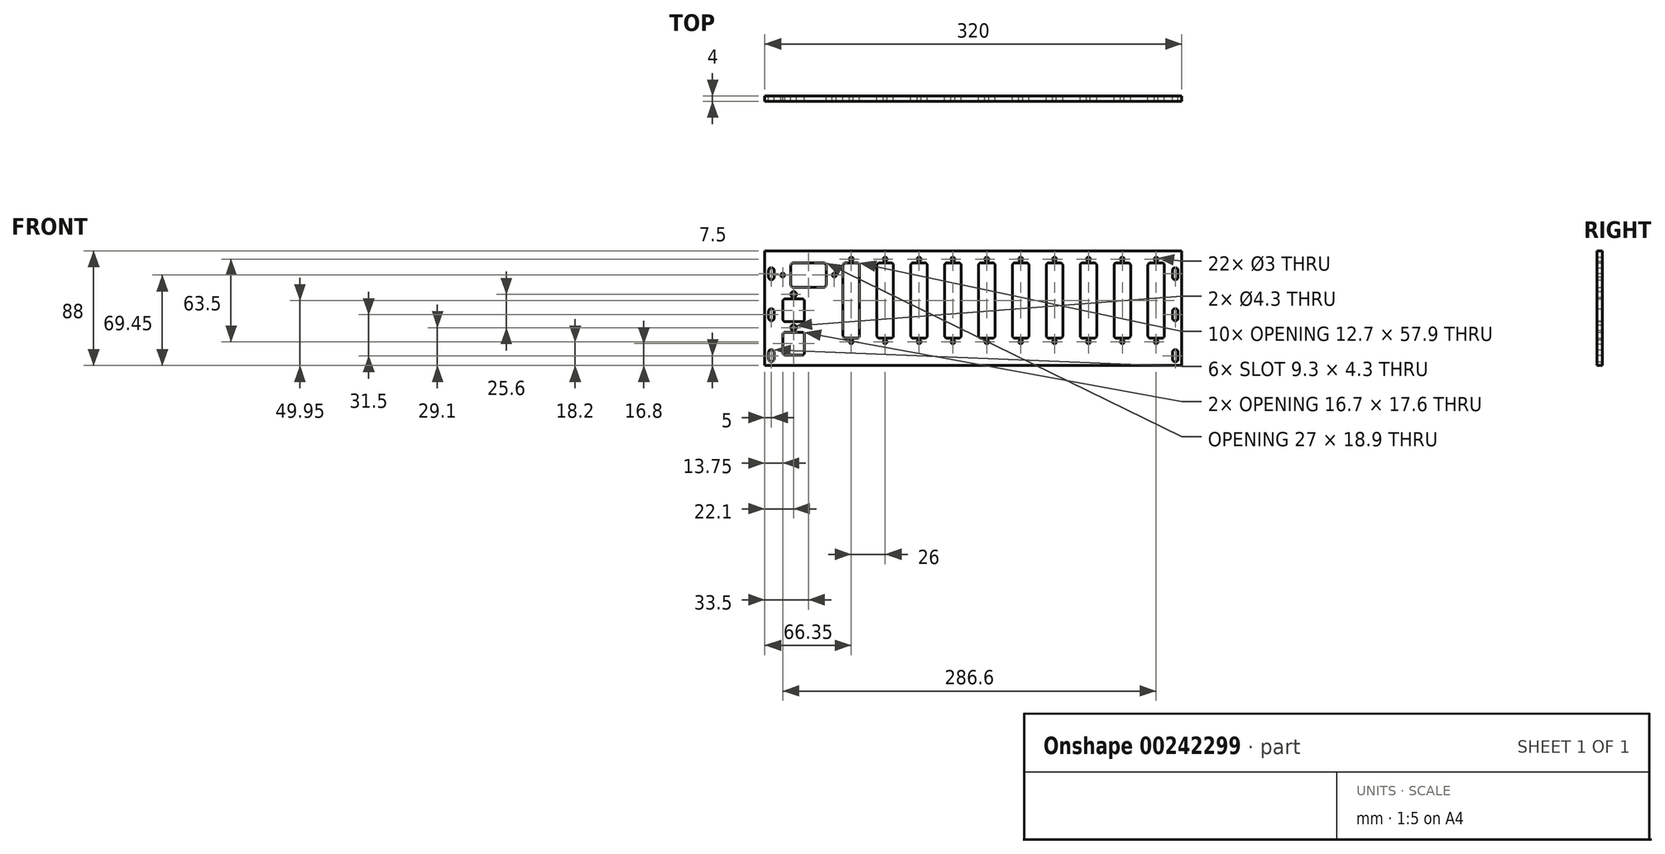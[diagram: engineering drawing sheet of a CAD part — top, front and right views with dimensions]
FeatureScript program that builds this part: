
annotation { "Feature Type Name" : "Feature", "Feature Type Description" : "" }
export const myFeature = defineFeature(function(context is Context, id is Id, definition is map)
    precondition{}
    {
        {
            var Q0;
            Q0=qCreatedBy(makeId("Front.planeOp"),FACE);
            var sketch = newSketch(context, id + "F0", { "sketchPlane" : qUnion([Q0])});
            skLineSegment(sketch, "E0.bottom", {"start": v(160, -44) * mm, "end": v(-160, -44) * mm});
            skLineSegment(sketch, "E0.top", {"start": v(160, 44) * mm, "end": v(-160, 44) * mm});
            skLineSegment(sketch, "E0.left", {"start": v(160, -44) * mm, "end": v(160, 44) * mm});
            skLineSegment(sketch, "E0.right", {"start": v(-160, -44) * mm, "end": v(-160, 44) * mm});
            skPoint(sketch, "E0.middle", {"position": v(0, 0) * mm});
            skLineSegment(sketch, "E1.bottom", {"start": v(-131.55, -36) * mm, "end": v(-144.25, -36) * mm});
            skLineSegment(sketch, "E1.top", {"start": v(-131.55, -18.4) * mm, "end": v(-144.25, -18.4) * mm});
            skLineSegment(sketch, "E1.left", {"start": v(-129.55, -34) * mm, "end": v(-129.55, -20.4) * mm});
            skLineSegment(sketch, "E1.right", {"start": v(-146.25, -34) * mm, "end": v(-146.25, -20.4) * mm});
            skPoint(sketch, "E1.middle", {"position": v(-137.9, -27.2) * mm});
            skLineSegment(sketch, "E2.0.1.0", {"start": v(-131.55, 7.2) * mm, "end": v(-144.25, 7.2) * mm});
            skLineSegment(sketch, "E2.0.1.1", {"start": v(-129.55, -8.4) * mm, "end": v(-129.55, 5.2) * mm});
            skLineSegment(sketch, "E2.0.1.2", {"start": v(-131.55, -10.4) * mm, "end": v(-144.25, -10.4) * mm});
            skLineSegment(sketch, "E2.0.1.3", {"start": v(-146.25, -8.4) * mm, "end": v(-146.25, 5.2) * mm});
            skLineSegment(sketch, "E2.direction1", {"start": v(-146.25, -18.4) * mm, "end": v(-121.25, -18.4) * mm, "construction": true});
            skLineSegment(sketch, "E2.direction2", {"start": v(-146.25, -18.4) * mm, "end": v(-146.25, 7.2) * mm, "construction": true});
            skLineSegment(sketch, "E3.bottom", {"start": v(-115, 16) * mm, "end": v(-138, 16) * mm});
            skLineSegment(sketch, "E3.top", {"start": v(-115, 34.9) * mm, "end": v(-138, 34.9) * mm});
            skLineSegment(sketch, "E3.left", {"start": v(-113, 18) * mm, "end": v(-113, 32.9) * mm});
            skLineSegment(sketch, "E3.right", {"start": v(-140, 18) * mm, "end": v(-140, 32.9) * mm});
            skPoint(sketch, "E3.middle", {"position": v(-126.5, 25.45) * mm});
            skCircle(sketch, "E4", {"center": v(-146.25, 25.45) * mm, "radius": 1.5 * mm});
            skCircle(sketch, "E5", {"center": v(-106.75, 25.45) * mm, "radius": 1.5 * mm});
            skLineSegment(sketch, "E6.bottom", {"start": v(-98, -23) * mm, "end": v(-89.3, -23) * mm});
            skLineSegment(sketch, "E6.top", {"start": v(-98, 34.9) * mm, "end": v(-89.3, 34.9) * mm});
            skLineSegment(sketch, "E6.left", {"start": v(-100, -21) * mm, "end": v(-100, 32.9) * mm});
            skLineSegment(sketch, "E6.right", {"start": v(-87.3, -21) * mm, "end": v(-87.3, 32.9) * mm});
            skCircle(sketch, "E7", {"center": v(-93.65, -25.8) * mm, "radius": 1.5 * mm});
            skPoint(sketch, "E7.centerSnap0", {"position": v(-93.65, -23) * mm});
            skCircle(sketch, "E8", {"center": v(-93.65, 37.7) * mm, "radius": 1.5 * mm});
            skPoint(sketch, "E8.centerSnap0", {"position": v(-93.65, 34.9) * mm});
            skCircle(sketch, "E9.1.0.0", {"center": v(-67.65, 37.7) * mm, "radius": 1.5 * mm});
            skLineSegment(sketch, "E9.1.0.1", {"start": v(-72, 34.9) * mm, "end": v(-63.3, 34.9) * mm});
            skLineSegment(sketch, "E9.1.0.2", {"start": v(-74, -21) * mm, "end": v(-74, 32.9) * mm});
            skLineSegment(sketch, "E9.1.0.3", {"start": v(-61.3, -21) * mm, "end": v(-61.3, 32.9) * mm});
            skLineSegment(sketch, "E9.1.0.4", {"start": v(-72, -23) * mm, "end": v(-63.3, -23) * mm});
            skCircle(sketch, "E9.1.0.5", {"center": v(-67.65, -25.8) * mm, "radius": 1.5 * mm});
            skCircle(sketch, "E9.2.0.0", {"center": v(-41.65, 37.7) * mm, "radius": 1.5 * mm});
            skLineSegment(sketch, "E9.2.0.1", {"start": v(-46, 34.9) * mm, "end": v(-37.3, 34.9) * mm});
            skLineSegment(sketch, "E9.2.0.2", {"start": v(-48, -21) * mm, "end": v(-48, 32.9) * mm});
            skLineSegment(sketch, "E9.2.0.3", {"start": v(-35.3, -21) * mm, "end": v(-35.3, 32.9) * mm});
            skLineSegment(sketch, "E9.2.0.4", {"start": v(-46, -23) * mm, "end": v(-37.3, -23) * mm});
            skCircle(sketch, "E9.2.0.5", {"center": v(-41.65, -25.8) * mm, "radius": 1.5 * mm});
            skCircle(sketch, "E9.3.0.0", {"center": v(-15.65, 37.7) * mm, "radius": 1.5 * mm});
            skLineSegment(sketch, "E9.3.0.1", {"start": v(-20, 34.9) * mm, "end": v(-11.3, 34.9) * mm});
            skLineSegment(sketch, "E9.3.0.2", {"start": v(-22, -21) * mm, "end": v(-22, 32.9) * mm});
            skLineSegment(sketch, "E9.3.0.3", {"start": v(-9.3, -21) * mm, "end": v(-9.3, 32.9) * mm});
            skLineSegment(sketch, "E9.3.0.4", {"start": v(-20, -23) * mm, "end": v(-11.3, -23) * mm});
            skCircle(sketch, "E9.3.0.5", {"center": v(-15.65, -25.8) * mm, "radius": 1.5 * mm});
            skCircle(sketch, "E9.4.0.0", {"center": v(10.35, 37.7) * mm, "radius": 1.5 * mm});
            skLineSegment(sketch, "E9.4.0.1", {"start": v(6, 34.9) * mm, "end": v(14.7, 34.9) * mm});
            skLineSegment(sketch, "E9.4.0.2", {"start": v(4, -21) * mm, "end": v(4, 32.9) * mm});
            skLineSegment(sketch, "E9.4.0.3", {"start": v(16.7, -21) * mm, "end": v(16.7, 32.9) * mm});
            skLineSegment(sketch, "E9.4.0.4", {"start": v(6, -23) * mm, "end": v(14.7, -23) * mm});
            skCircle(sketch, "E9.4.0.5", {"center": v(10.35, -25.8) * mm, "radius": 1.5 * mm});
            skCircle(sketch, "E9.5.0.0", {"center": v(36.35, 37.7) * mm, "radius": 1.5 * mm});
            skLineSegment(sketch, "E9.5.0.1", {"start": v(32, 34.9) * mm, "end": v(40.7, 34.9) * mm});
            skLineSegment(sketch, "E9.5.0.2", {"start": v(30, -21) * mm, "end": v(30, 32.9) * mm});
            skLineSegment(sketch, "E9.5.0.3", {"start": v(42.7, -21) * mm, "end": v(42.7, 32.9) * mm});
            skLineSegment(sketch, "E9.5.0.4", {"start": v(32, -23) * mm, "end": v(40.7, -23) * mm});
            skCircle(sketch, "E9.5.0.5", {"center": v(36.35, -25.8) * mm, "radius": 1.5 * mm});
            skCircle(sketch, "E9.6.0.0", {"center": v(62.35, 37.7) * mm, "radius": 1.5 * mm});
            skLineSegment(sketch, "E9.6.0.1", {"start": v(58, 34.9) * mm, "end": v(66.7, 34.9) * mm});
            skLineSegment(sketch, "E9.6.0.2", {"start": v(56, -21) * mm, "end": v(56, 32.9) * mm});
            skLineSegment(sketch, "E9.6.0.3", {"start": v(68.7, -21) * mm, "end": v(68.7, 32.9) * mm});
            skLineSegment(sketch, "E9.6.0.4", {"start": v(58, -23) * mm, "end": v(66.7, -23) * mm});
            skCircle(sketch, "E9.6.0.5", {"center": v(62.35, -25.8) * mm, "radius": 1.5 * mm});
            skCircle(sketch, "E9.7.0.0", {"center": v(88.35, 37.7) * mm, "radius": 1.5 * mm});
            skLineSegment(sketch, "E9.7.0.1", {"start": v(84, 34.9) * mm, "end": v(92.7, 34.9) * mm});
            skLineSegment(sketch, "E9.7.0.2", {"start": v(82, -21) * mm, "end": v(82, 32.9) * mm});
            skLineSegment(sketch, "E9.7.0.3", {"start": v(94.7, -21) * mm, "end": v(94.7, 32.9) * mm});
            skLineSegment(sketch, "E9.7.0.4", {"start": v(84, -23) * mm, "end": v(92.7, -23) * mm});
            skCircle(sketch, "E9.7.0.5", {"center": v(88.35, -25.8) * mm, "radius": 1.5 * mm});
            skCircle(sketch, "E9.8.0.0", {"center": v(114.35, 37.7) * mm, "radius": 1.5 * mm});
            skLineSegment(sketch, "E9.8.0.1", {"start": v(110, 34.9) * mm, "end": v(118.7, 34.9) * mm});
            skLineSegment(sketch, "E9.8.0.2", {"start": v(108, -21) * mm, "end": v(108, 32.9) * mm});
            skLineSegment(sketch, "E9.8.0.3", {"start": v(120.7, -21) * mm, "end": v(120.7, 32.9) * mm});
            skLineSegment(sketch, "E9.8.0.4", {"start": v(110, -23) * mm, "end": v(118.7, -23) * mm});
            skCircle(sketch, "E9.8.0.5", {"center": v(114.35, -25.8) * mm, "radius": 1.5 * mm});
            skCircle(sketch, "E9.9.0.0", {"center": v(140.35, 37.7) * mm, "radius": 1.5 * mm});
            skLineSegment(sketch, "E9.9.0.1", {"start": v(136, 34.9) * mm, "end": v(144.7, 34.9) * mm});
            skLineSegment(sketch, "E9.9.0.2", {"start": v(134, -21) * mm, "end": v(134, 32.9) * mm});
            skLineSegment(sketch, "E9.9.0.3", {"start": v(146.7, -21) * mm, "end": v(146.7, 32.9) * mm});
            skLineSegment(sketch, "E9.9.0.4", {"start": v(136, -23) * mm, "end": v(144.7, -23) * mm});
            skCircle(sketch, "E9.9.0.5", {"center": v(140.35, -25.8) * mm, "radius": 1.5 * mm});
            skLineSegment(sketch, "E9.direction1", {"start": v(-93.65, 37.7) * mm, "end": v(-67.65, 37.7) * mm, "construction": true});
            skPoint(sketch, "E10.visualSharp", {"position": v(-100, 34.9) * mm});
            skArc(sketch, "E10.filletArc", {"start": v(-98, 34.9) * mm, "mid": v(-99.41, 34.31) * mm, "end": v(-100, 32.9) * mm});
            skPoint(sketch, "E11.visualSharp", {"position": v(-87.3, 34.9) * mm});
            skArc(sketch, "E11.filletArc", {"start": v(-87.3, 32.9) * mm, "mid": v(-87.89, 34.31) * mm, "end": v(-89.3, 34.9) * mm});
            skPoint(sketch, "E12.visualSharp", {"position": v(-100, -23) * mm});
            skArc(sketch, "E12.filletArc", {"start": v(-100, -21) * mm, "mid": v(-99.41, -22.41) * mm, "end": v(-98, -23) * mm});
            skPoint(sketch, "E13.visualSharp", {"position": v(-87.3, -23) * mm});
            skArc(sketch, "E13.filletArc", {"start": v(-89.3, -23) * mm, "mid": v(-87.89, -22.41) * mm, "end": v(-87.3, -21) * mm});
            skPoint(sketch, "E14.visualSharp", {"position": v(-74, 34.9) * mm});
            skArc(sketch, "E14.filletArc", {"start": v(-72, 34.9) * mm, "mid": v(-73.41, 34.31) * mm, "end": v(-74, 32.9) * mm});
            skPoint(sketch, "E15.visualSharp", {"position": v(-61.3, 34.9) * mm});
            skArc(sketch, "E15.filletArc", {"start": v(-61.3, 32.9) * mm, "mid": v(-61.89, 34.31) * mm, "end": v(-63.3, 34.9) * mm});
            skPoint(sketch, "E16.visualSharp", {"position": v(-61.3, -23) * mm});
            skArc(sketch, "E16.filletArc", {"start": v(-63.3, -23) * mm, "mid": v(-61.89, -22.41) * mm, "end": v(-61.3, -21) * mm});
            skPoint(sketch, "E17.visualSharp", {"position": v(-74, -23) * mm});
            skArc(sketch, "E17.filletArc", {"start": v(-74, -21) * mm, "mid": v(-73.41, -22.41) * mm, "end": v(-72, -23) * mm});
            skPoint(sketch, "E18.visualSharp", {"position": v(-48, 34.9) * mm});
            skArc(sketch, "E18.filletArc", {"start": v(-46, 34.9) * mm, "mid": v(-47.41, 34.31) * mm, "end": v(-48, 32.9) * mm});
            skPoint(sketch, "E19.visualSharp", {"position": v(-35.3, 34.9) * mm});
            skArc(sketch, "E19.filletArc", {"start": v(-35.3, 32.9) * mm, "mid": v(-35.89, 34.31) * mm, "end": v(-37.3, 34.9) * mm});
            skPoint(sketch, "E20.visualSharp", {"position": v(-35.3, -23) * mm});
            skArc(sketch, "E20.filletArc", {"start": v(-37.3, -23) * mm, "mid": v(-35.89, -22.41) * mm, "end": v(-35.3, -21) * mm});
            skPoint(sketch, "E21.visualSharp", {"position": v(-48, -23) * mm});
            skArc(sketch, "E21.filletArc", {"start": v(-48, -21) * mm, "mid": v(-47.41, -22.41) * mm, "end": v(-46, -23) * mm});
            skPoint(sketch, "E22.visualSharp", {"position": v(-22, -23) * mm});
            skArc(sketch, "E22.filletArc", {"start": v(-22, -21) * mm, "mid": v(-21.41, -22.41) * mm, "end": v(-20, -23) * mm});
            skPoint(sketch, "E23.visualSharp", {"position": v(-9.3, -23) * mm});
            skArc(sketch, "E23.filletArc", {"start": v(-11.3, -23) * mm, "mid": v(-9.89, -22.41) * mm, "end": v(-9.3, -21) * mm});
            skPoint(sketch, "E24.visualSharp", {"position": v(-9.3, 34.9) * mm});
            skArc(sketch, "E24.filletArc", {"start": v(-9.3, 32.9) * mm, "mid": v(-9.89, 34.31) * mm, "end": v(-11.3, 34.9) * mm});
            skPoint(sketch, "E25.visualSharp", {"position": v(-22, 34.9) * mm});
            skArc(sketch, "E25.filletArc", {"start": v(-20, 34.9) * mm, "mid": v(-21.41, 34.31) * mm, "end": v(-22, 32.9) * mm});
            skPoint(sketch, "E26.visualSharp", {"position": v(4, 34.9) * mm});
            skArc(sketch, "E26.filletArc", {"start": v(6, 34.9) * mm, "mid": v(4.59, 34.31) * mm, "end": v(4, 32.9) * mm});
            skPoint(sketch, "E27.visualSharp", {"position": v(16.7, 34.9) * mm});
            skArc(sketch, "E27.filletArc", {"start": v(16.7, 32.9) * mm, "mid": v(16.11, 34.31) * mm, "end": v(14.7, 34.9) * mm});
            skPoint(sketch, "E28.visualSharp", {"position": v(16.7, -23) * mm});
            skArc(sketch, "E28.filletArc", {"start": v(14.7, -23) * mm, "mid": v(16.11, -22.41) * mm, "end": v(16.7, -21) * mm});
            skPoint(sketch, "E29.visualSharp", {"position": v(4, -23) * mm});
            skArc(sketch, "E29.filletArc", {"start": v(4, -21) * mm, "mid": v(4.59, -22.41) * mm, "end": v(6, -23) * mm});
            skPoint(sketch, "E30.visualSharp", {"position": v(30, 34.9) * mm});
            skArc(sketch, "E30.filletArc", {"start": v(32, 34.9) * mm, "mid": v(30.59, 34.31) * mm, "end": v(30, 32.9) * mm});
            skPoint(sketch, "E31.visualSharp", {"position": v(42.7, 34.9) * mm});
            skArc(sketch, "E31.filletArc", {"start": v(42.7, 32.9) * mm, "mid": v(42.11, 34.31) * mm, "end": v(40.7, 34.9) * mm});
            skPoint(sketch, "E32.visualSharp", {"position": v(42.7, -23) * mm});
            skArc(sketch, "E32.filletArc", {"start": v(40.7, -23) * mm, "mid": v(42.11, -22.41) * mm, "end": v(42.7, -21) * mm});
            skPoint(sketch, "E33.visualSharp", {"position": v(30, -23) * mm});
            skArc(sketch, "E33.filletArc", {"start": v(30, -21) * mm, "mid": v(30.59, -22.41) * mm, "end": v(32, -23) * mm});
            skPoint(sketch, "E34.visualSharp", {"position": v(56, 34.9) * mm});
            skArc(sketch, "E34.filletArc", {"start": v(58, 34.9) * mm, "mid": v(56.59, 34.31) * mm, "end": v(56, 32.9) * mm});
            skPoint(sketch, "E35.visualSharp", {"position": v(68.7, 34.9) * mm});
            skArc(sketch, "E35.filletArc", {"start": v(68.7, 32.9) * mm, "mid": v(68.11, 34.31) * mm, "end": v(66.7, 34.9) * mm});
            skPoint(sketch, "E36.visualSharp", {"position": v(68.7, -23) * mm});
            skArc(sketch, "E36.filletArc", {"start": v(66.7, -23) * mm, "mid": v(68.11, -22.41) * mm, "end": v(68.7, -21) * mm});
            skPoint(sketch, "E37.visualSharp", {"position": v(56, -23) * mm});
            skArc(sketch, "E37.filletArc", {"start": v(56, -21) * mm, "mid": v(56.59, -22.41) * mm, "end": v(58, -23) * mm});
            skPoint(sketch, "E38.visualSharp", {"position": v(146.7, -23) * mm});
            skArc(sketch, "E38.filletArc", {"start": v(144.7, -23) * mm, "mid": v(146.11, -22.41) * mm, "end": v(146.7, -21) * mm});
            skPoint(sketch, "E39.visualSharp", {"position": v(146.7, 34.9) * mm});
            skArc(sketch, "E39.filletArc", {"start": v(146.7, 32.9) * mm, "mid": v(146.11, 34.31) * mm, "end": v(144.7, 34.9) * mm});
            skPoint(sketch, "E40.visualSharp", {"position": v(134, 34.9) * mm});
            skArc(sketch, "E40.filletArc", {"start": v(136, 34.9) * mm, "mid": v(134.59, 34.31) * mm, "end": v(134, 32.9) * mm});
            skPoint(sketch, "E41.visualSharp", {"position": v(134, -23) * mm});
            skArc(sketch, "E41.filletArc", {"start": v(134, -21) * mm, "mid": v(134.59, -22.41) * mm, "end": v(136, -23) * mm});
            skPoint(sketch, "E42.visualSharp", {"position": v(120.7, -23) * mm});
            skArc(sketch, "E42.filletArc", {"start": v(118.7, -23) * mm, "mid": v(120.11, -22.41) * mm, "end": v(120.7, -21) * mm});
            skPoint(sketch, "E43.visualSharp", {"position": v(108, -23) * mm});
            skArc(sketch, "E43.filletArc", {"start": v(108, -21) * mm, "mid": v(108.59, -22.41) * mm, "end": v(110, -23) * mm});
            skPoint(sketch, "E44.visualSharp", {"position": v(82, -23) * mm});
            skArc(sketch, "E44.filletArc", {"start": v(82, -21) * mm, "mid": v(82.59, -22.41) * mm, "end": v(84, -23) * mm});
            skPoint(sketch, "E45.visualSharp", {"position": v(82, 34.9) * mm});
            skArc(sketch, "E45.filletArc", {"start": v(84, 34.9) * mm, "mid": v(82.59, 34.31) * mm, "end": v(82, 32.9) * mm});
            skPoint(sketch, "E46.visualSharp", {"position": v(108, 34.9) * mm});
            skArc(sketch, "E46.filletArc", {"start": v(110, 34.9) * mm, "mid": v(108.59, 34.31) * mm, "end": v(108, 32.9) * mm});
            skPoint(sketch, "E47.visualSharp", {"position": v(120.7, 34.9) * mm});
            skArc(sketch, "E47.filletArc", {"start": v(120.7, 32.9) * mm, "mid": v(120.11, 34.31) * mm, "end": v(118.7, 34.9) * mm});
            skPoint(sketch, "E48.visualSharp", {"position": v(94.7, 34.9) * mm});
            skArc(sketch, "E48.filletArc", {"start": v(94.7, 32.9) * mm, "mid": v(94.11, 34.31) * mm, "end": v(92.7, 34.9) * mm});
            skPoint(sketch, "E49.visualSharp", {"position": v(94.7, -23) * mm});
            skArc(sketch, "E49.filletArc", {"start": v(92.7, -23) * mm, "mid": v(94.11, -22.41) * mm, "end": v(94.7, -21) * mm});
            skPoint(sketch, "E50.visualSharp", {"position": v(-113, 34.9) * mm});
            skArc(sketch, "E50.filletArc", {"start": v(-113, 32.9) * mm, "mid": v(-113.59, 34.31) * mm, "end": v(-115, 34.9) * mm});
            skPoint(sketch, "E51.visualSharp", {"position": v(-140, 34.9) * mm});
            skArc(sketch, "E51.filletArc", {"start": v(-138, 34.9) * mm, "mid": v(-139.41, 34.31) * mm, "end": v(-140, 32.9) * mm});
            skPoint(sketch, "E52.visualSharp", {"position": v(-140, 16) * mm});
            skArc(sketch, "E52.filletArc", {"start": v(-140, 18) * mm, "mid": v(-139.41, 16.59) * mm, "end": v(-138, 16) * mm});
            skPoint(sketch, "E53.visualSharp", {"position": v(-113, 16) * mm});
            skArc(sketch, "E53.filletArc", {"start": v(-115, 16) * mm, "mid": v(-113.59, 16.59) * mm, "end": v(-113, 18) * mm});
            skPoint(sketch, "E54.visualSharp", {"position": v(-129.55, 7.2) * mm});
            skArc(sketch, "E54.filletArc", {"start": v(-129.55, 5.2) * mm, "mid": v(-130.14, 6.61) * mm, "end": v(-131.55, 7.2) * mm});
            skPoint(sketch, "E55.visualSharp", {"position": v(-146.25, 7.2) * mm});
            skArc(sketch, "E55.filletArc", {"start": v(-144.25, 7.2) * mm, "mid": v(-145.66, 6.61) * mm, "end": v(-146.25, 5.2) * mm});
            skPoint(sketch, "E56.visualSharp", {"position": v(-146.25, -10.4) * mm});
            skArc(sketch, "E56.filletArc", {"start": v(-146.25, -8.4) * mm, "mid": v(-145.66, -9.81) * mm, "end": v(-144.25, -10.4) * mm});
            skPoint(sketch, "E57.visualSharp", {"position": v(-129.55, -10.4) * mm});
            skArc(sketch, "E57.filletArc", {"start": v(-131.55, -10.4) * mm, "mid": v(-130.14, -9.81) * mm, "end": v(-129.55, -8.4) * mm});
            skPoint(sketch, "E58.visualSharp", {"position": v(-129.55, -18.4) * mm});
            skArc(sketch, "E58.filletArc", {"start": v(-129.55, -20.4) * mm, "mid": v(-130.14, -18.99) * mm, "end": v(-131.55, -18.4) * mm});
            skPoint(sketch, "E59.visualSharp", {"position": v(-146.25, -18.4) * mm});
            skArc(sketch, "E59.filletArc", {"start": v(-144.25, -18.4) * mm, "mid": v(-145.66, -18.99) * mm, "end": v(-146.25, -20.4) * mm});
            skPoint(sketch, "E60.visualSharp", {"position": v(-146.25, -36) * mm});
            skArc(sketch, "E60.filletArc", {"start": v(-146.25, -34) * mm, "mid": v(-145.66, -35.41) * mm, "end": v(-144.25, -36) * mm});
            skPoint(sketch, "E61.visualSharp", {"position": v(-129.55, -36) * mm});
            skArc(sketch, "E61.filletArc", {"start": v(-131.55, -36) * mm, "mid": v(-130.14, -35.41) * mm, "end": v(-129.55, -34) * mm});
            skLineSegment(sketch, "E62", {"start": v(-152.85, -39) * mm, "end": v(-152.85, -34) * mm});
            skLineSegment(sketch, "E63", {"start": v(-157.15, -34) * mm, "end": v(-157.15, -39) * mm});
            skArc(sketch, "E64", {"start": v(-152.85, -34) * mm, "mid": v(-155, -31.85) * mm, "end": v(-157.15, -34) * mm});
            skArc(sketch, "E65", {"start": v(-157.15, -39) * mm, "mid": v(-155, -41.15) * mm, "end": v(-152.85, -39) * mm});
            skLineSegment(sketch, "E66.0.1.0", {"start": v(-152.85, -7.5) * mm, "end": v(-152.85, -2.5) * mm});
            skArc(sketch, "E66.0.1.1", {"start": v(-152.85, -2.5) * mm, "mid": v(-155, -0.35) * mm, "end": v(-157.15, -2.5) * mm});
            skLineSegment(sketch, "E66.0.1.2", {"start": v(-157.15, -2.5) * mm, "end": v(-157.15, -7.5) * mm});
            skArc(sketch, "E66.0.1.3", {"start": v(-157.15, -7.5) * mm, "mid": v(-155, -9.65) * mm, "end": v(-152.85, -7.5) * mm});
            skLineSegment(sketch, "E66.1.0.0", {"start": v(157.15, -39) * mm, "end": v(157.15, -34) * mm});
            skArc(sketch, "E66.1.0.1", {"start": v(157.15, -34) * mm, "mid": v(155, -31.85) * mm, "end": v(152.85, -34) * mm});
            skLineSegment(sketch, "E66.1.0.2", {"start": v(152.85, -34) * mm, "end": v(152.85, -39) * mm});
            skArc(sketch, "E66.1.0.3", {"start": v(152.85, -39) * mm, "mid": v(155, -41.15) * mm, "end": v(157.15, -39) * mm});
            skLineSegment(sketch, "E66.1.1.0", {"start": v(157.15, -7.5) * mm, "end": v(157.15, -2.5) * mm});
            skArc(sketch, "E66.1.1.1", {"start": v(157.15, -2.5) * mm, "mid": v(155, -0.35) * mm, "end": v(152.85, -2.5) * mm});
            skLineSegment(sketch, "E66.1.1.2", {"start": v(152.85, -2.5) * mm, "end": v(152.85, -7.5) * mm});
            skArc(sketch, "E66.1.1.3", {"start": v(152.85, -7.5) * mm, "mid": v(155, -9.65) * mm, "end": v(157.15, -7.5) * mm});
            skLineSegment(sketch, "E66.direction1", {"start": v(-152.85, -39) * mm, "end": v(157.15, -39) * mm, "construction": true});
            skLineSegment(sketch, "E66.direction2", {"start": v(-152.85, -39) * mm, "end": v(-152.85, -7.5) * mm, "construction": true});
            skCircle(sketch, "E67", {"center": v(-137.9, -14.9) * mm, "radius": 2.15 * mm});
            skCircle(sketch, "E68.0.1.0", {"center": v(-137.9, 10.7) * mm, "radius": 2.15 * mm});
            skLineSegment(sketch, "E68.direction1", {"start": v(-137.9, -14.9) * mm, "end": v(-128.2, -14.9) * mm, "construction": true});
            skLineSegment(sketch, "E68.direction2", {"start": v(-137.9, -14.9) * mm, "end": v(-137.9, 10.7) * mm, "construction": true});
            skLineSegment(sketch, "E69.0.0.2", {"start": v(-152.85, 24) * mm, "end": v(-152.85, 29) * mm});
            skArc(sketch, "E69.3.0.2", {"start": v(-152.85, 29) * mm, "mid": v(-155, 31.15) * mm, "end": v(-157.15, 29) * mm});
            skLineSegment(sketch, "E69.7.0.2", {"start": v(-157.15, 29) * mm, "end": v(-157.15, 24) * mm});
            skArc(sketch, "E69.10.0.2", {"start": v(-157.15, 24) * mm, "mid": v(-155, 21.85) * mm, "end": v(-152.85, 24) * mm});
            skLineSegment(sketch, "E69.0.1.2", {"start": v(157.15, 24) * mm, "end": v(157.15, 29) * mm});
            skArc(sketch, "E69.3.1.2", {"start": v(157.15, 29) * mm, "mid": v(155, 31.15) * mm, "end": v(152.85, 29) * mm});
            skLineSegment(sketch, "E69.7.1.2", {"start": v(152.85, 29) * mm, "end": v(152.85, 24) * mm});
            skArc(sketch, "E69.10.1.2", {"start": v(152.85, 24) * mm, "mid": v(155, 21.85) * mm, "end": v(157.15, 24) * mm});
            skSolve(sketch);
        }
        {
            var Q0;
            Q0=makeQuery(id+"F0.imprint","IMPRINT",FACE,{"disambiguationData":[TD([[makeQuery(id+"F0.imprint","IMPRINT",EDGE,{"derivedFrom":sQuery(id+"F0.wireOp",EDGE,"E0.bottom")}),-1.0]])]});
            extrude(context, id + "F1", {"entities" : qUnion([Q0]), "depth" : 4 * mm});
        }
    });
